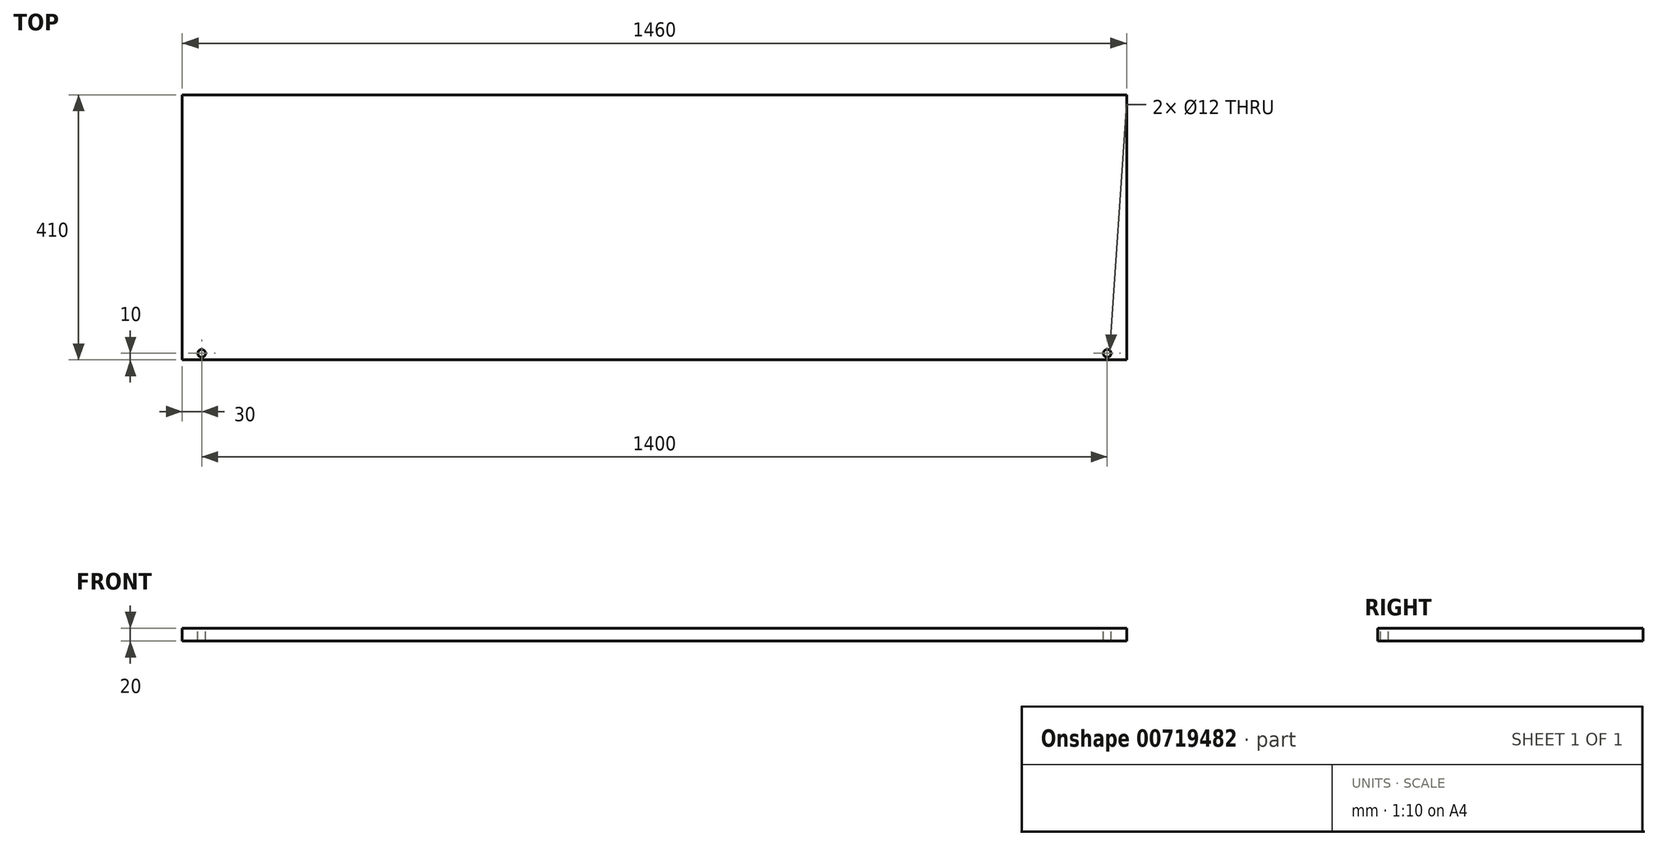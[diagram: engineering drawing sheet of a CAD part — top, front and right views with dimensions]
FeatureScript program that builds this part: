
annotation { "Feature Type Name" : "Feature", "Feature Type Description" : "" }
export const myFeature = defineFeature(function(context is Context, id is Id, definition is map)
    precondition{}
    {
        {
            var Q0;
            Q0=qCreatedBy(makeId("Top.planeOp"),FACE);
            var sketch = newSketch(context, id + "F0", { "sketchPlane" : qUnion([Q0])});
            skLineSegment(sketch, "E0.bottom", {"start": v(730, 205) * mm, "end": v(-730, 205) * mm});
            skLineSegment(sketch, "E0.top", {"start": v(730, -205) * mm, "end": v(-730, -205) * mm});
            skLineSegment(sketch, "E0.left", {"start": v(730, 205) * mm, "end": v(730, -205) * mm});
            skLineSegment(sketch, "E0.right", {"start": v(-730, 205) * mm, "end": v(-730, -205) * mm});
            skPoint(sketch, "E0.middle", {"position": v(0, 0) * mm});
            skSolve(sketch);
        }
        {
            var Q0;
            Q0=makeQuery(id+"F0.imprint","IMPRINT",FACE,{"disambiguationData":[TD([[makeQuery(id+"F0.imprint","IMPRINT",EDGE,{"derivedFrom":sQuery(id+"F0.wireOp",EDGE,"E0.bottom")}),1.0]])]});
            extrude(context, id + "F1", {"entities" : qUnion([Q0]), "depth" : 20 * mm, "offsetDistance" : 25 * mm});
        }
        {
            var Q0;
            Q0=makeQuery(id+"F1.opExtrude","CAP_FACE",FACE,{"disambiguationData":[OSD([sQuery(id+"F0.wireOp",EDGE,"E0.bottom"),sQuery(id+"F0.wireOp",EDGE,"E0.top"),sQuery(id+"F0.wireOp",EDGE,"E0.left"),sQuery(id+"F0.wireOp",EDGE,"E0.right")])],"isStart":false});
            var sketch = newSketch(context, id + "F2", { "sketchPlane" : qUnion([Q0])});
            skLineSegment(sketch, "E1", {"start": v(0, 0) * mm, "end": v(0, -195) * mm, "construction": true});
            skLineSegment(sketch, "E2", {"start": v(-700, -195) * mm, "end": v(700, -195) * mm, "construction": true});
            skCircle(sketch, "E3", {"center": v(-700, -195) * mm, "radius": 6 * mm});
            skCircle(sketch, "E4", {"center": v(700, -195) * mm, "radius": 6 * mm});
            skSolve(sketch);
        }
        {
            var Q0;
            Q0 = qSketchRegion(id + "F2", true);
            extrude(context, id + "F3", {"entities" : qUnion([Q0]), "operationType" : NewBodyOperationType.REMOVE, "endBound" : BoundingType.THROUGH_ALL, "oppositeDirection" : true, "depth" : 25 * mm, "offsetDistance" : 25 * mm});
        }
    });
